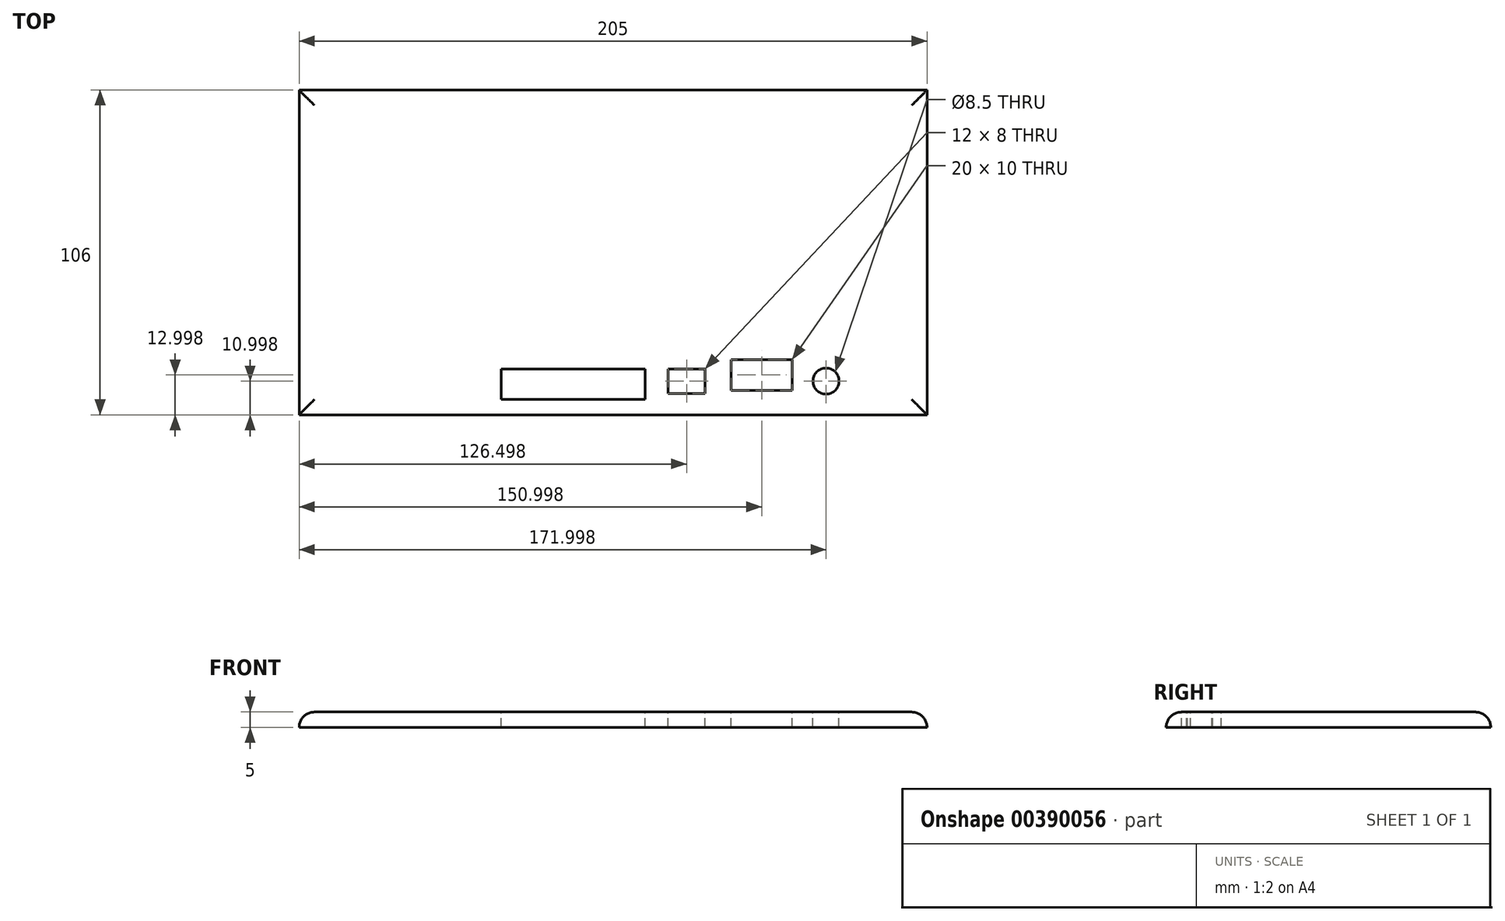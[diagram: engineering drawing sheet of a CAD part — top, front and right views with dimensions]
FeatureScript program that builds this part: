
annotation { "Feature Type Name" : "Feature", "Feature Type Description" : "" }
export const myFeature = defineFeature(function(context is Context, id is Id, definition is map)
    precondition{}
    {
        {
            var Q0;
            Q0=qCreatedBy(makeId("Top.planeOp"),FACE);
            var sketch = newSketch(context, id + "F0", { "sketchPlane" : qUnion([Q0])});
            skLineSegment(sketch, "E0.bottom", {"start": v(-821.61, -528.85) * mm, "end": v(-616.61, -528.85) * mm});
            skLineSegment(sketch, "E0.top", {"start": v(-821.61, -422.85) * mm, "end": v(-616.61, -422.85) * mm});
            skLineSegment(sketch, "E0.left", {"start": v(-821.61, -528.85) * mm, "end": v(-821.61, -422.85) * mm});
            skLineSegment(sketch, "E0.right", {"start": v(-616.61, -528.85) * mm, "end": v(-616.61, -422.85) * mm});
            skSolve(sketch);
        }
        {
            var Q0;
            Q0=makeQuery(id+"F0.imprint","IMPRINT",FACE,{"disambiguationData":[TD([[makeQuery(id+"F0.imprint","IMPRINT",EDGE,{"derivedFrom":sQuery(id+"F0.wireOp",EDGE,"E0.bottom")}),1.0]])]});
            extrude(context, id + "F1", {"entities" : qUnion([Q0]), "depth" : 5 * mm});
        }
        {
            var Q0;
            Q0=makeQuery(id+"F1.opExtrude","CAP_FACE",FACE,{"disambiguationData":[OSD([sQuery(id+"F0.wireOp",EDGE,"E0.bottom"),sQuery(id+"F0.wireOp",EDGE,"E0.top"),sQuery(id+"F0.wireOp",EDGE,"E0.left"),sQuery(id+"F0.wireOp",EDGE,"E0.right")])],"isStart":false});
            var sketch = newSketch(context, id + "F2", { "sketchPlane" : qUnion([Q0])});
            skCircle(sketch, "E1", {"center": v(-649.61, -517.85) * mm, "radius": 4.25 * mm});
            skSolve(sketch);
        }
        {
            var Q0;
            Q0=makeQuery(id+"F2.imprint","IMPRINT",FACE,{"disambiguationData":[TD([[makeQuery(id+"F2.imprint","IMPRINT",EDGE,{"derivedFrom":sQuery(id+"F2.wireOp",EDGE,"E1")}),1.0]])]});
            extrude(context, id + "F3", {"entities" : qUnion([Q0]), "operationType" : NewBodyOperationType.REMOVE, "oppositeDirection" : true, "depth" : 500 * mm});
        }
        {
            var Q0;
            Q0=makeQuery(id+"F1.opExtrude","CAP_FACE",FACE,{"disambiguationData":[OSD([sQuery(id+"F0.wireOp",EDGE,"E0.bottom"),sQuery(id+"F0.wireOp",EDGE,"E0.top"),sQuery(id+"F0.wireOp",EDGE,"E0.left"),sQuery(id+"F0.wireOp",EDGE,"E0.right")])],"isStart":false});
            var sketch = newSketch(context, id + "F4", { "sketchPlane" : qUnion([Q0])});
            skLineSegment(sketch, "E2.bottom", {"start": v(-680.61, -510.85) * mm, "end": v(-660.61, -510.85) * mm});
            skLineSegment(sketch, "E2.top", {"start": v(-680.61, -520.85) * mm, "end": v(-660.61, -520.85) * mm});
            skLineSegment(sketch, "E2.left", {"start": v(-680.61, -510.85) * mm, "end": v(-680.61, -520.85) * mm});
            skLineSegment(sketch, "E2.right", {"start": v(-660.61, -510.85) * mm, "end": v(-660.61, -520.85) * mm});
            skSolve(sketch);
        }
        {
            var Q0;
            Q0=makeQuery(id+"F4.imprint","IMPRINT",FACE,{"disambiguationData":[TD([[makeQuery(id+"F4.imprint","IMPRINT",EDGE,{"derivedFrom":sQuery(id+"F4.wireOp",EDGE,"E2.bottom")}),-1.0]])]});
            extrude(context, id + "F5", {"entities" : qUnion([Q0]), "operationType" : NewBodyOperationType.REMOVE, "oppositeDirection" : true, "depth" : 500 * mm});
        }
        {
            var Q0;
            Q0=makeQuery(id+"F1.opExtrude","CAP_FACE",FACE,{"disambiguationData":[OSD([sQuery(id+"F0.wireOp",EDGE,"E0.bottom"),sQuery(id+"F0.wireOp",EDGE,"E0.top"),sQuery(id+"F0.wireOp",EDGE,"E0.left"),sQuery(id+"F0.wireOp",EDGE,"E0.right")])],"isStart":false});
            var sketch = newSketch(context, id + "F6", { "sketchPlane" : qUnion([Q0])});
            skLineSegment(sketch, "E3.bottom", {"start": v(-701.11, -521.85) * mm, "end": v(-689.11, -521.85) * mm});
            skLineSegment(sketch, "E3.top", {"start": v(-701.11, -513.85) * mm, "end": v(-689.11, -513.85) * mm});
            skLineSegment(sketch, "E3.left", {"start": v(-701.11, -521.85) * mm, "end": v(-701.11, -513.85) * mm});
            skLineSegment(sketch, "E3.right", {"start": v(-689.11, -521.85) * mm, "end": v(-689.11, -513.85) * mm});
            skSolve(sketch);
        }
        {
            var Q0;
            Q0=makeQuery(id+"F6.imprint","IMPRINT",FACE,{"disambiguationData":[TD([[makeQuery(id+"F6.imprint","IMPRINT",EDGE,{"derivedFrom":sQuery(id+"F6.wireOp",EDGE,"E3.bottom")}),1.0]])]});
            extrude(context, id + "F7", {"entities" : qUnion([Q0]), "operationType" : NewBodyOperationType.REMOVE, "oppositeDirection" : true, "depth" : 500 * mm});
        }
        {
            var Q0;
            Q0=makeQuery(id+"F1.opExtrude","CAP_EDGE",EDGE,{"disambiguationData":[OSD([sQuery(id+"F0.wireOp",EDGE,"E0.left")])],"isStart":false});
            var Q1;
            Q1=makeQuery(id+"F1.opExtrude","CAP_EDGE",EDGE,{"disambiguationData":[OSD([sQuery(id+"F0.wireOp",EDGE,"E0.bottom")])],"isStart":false});
            var Q2;
            Q2=makeQuery(id+"F1.opExtrude","CAP_EDGE",EDGE,{"disambiguationData":[OSD([sQuery(id+"F0.wireOp",EDGE,"E0.right")])],"isStart":false});
            var Q3;
            Q3=makeQuery(id+"F1.opExtrude","CAP_EDGE",EDGE,{"disambiguationData":[OSD([sQuery(id+"F0.wireOp",EDGE,"E0.top")])],"isStart":false});
            fillet(context, id + "F8", {"entities" : qUnion([Q0, Q1, Q2, Q3]), "radius" : 5 * mm, "tangentPropagation" : true, "allowEdgeOverflow" : false});
        }
        {
            var Q0;
            Q0=makeQuery(id+"F1.opExtrude","CAP_FACE",FACE,{"disambiguationData":[OSD([sQuery(id+"F0.wireOp",EDGE,"E0.bottom"),sQuery(id+"F0.wireOp",EDGE,"E0.top"),sQuery(id+"F0.wireOp",EDGE,"E0.left"),sQuery(id+"F0.wireOp",EDGE,"E0.right")])],"isStart":false});
            var sketch = newSketch(context, id + "F9", { "sketchPlane" : qUnion([Q0])});
            skLineSegment(sketch, "E4.bottom", {"start": v(-755.61, -513.85) * mm, "end": v(-708.61, -513.85) * mm});
            skLineSegment(sketch, "E4.top", {"start": v(-755.61, -523.85) * mm, "end": v(-708.61, -523.85) * mm});
            skLineSegment(sketch, "E4.left", {"start": v(-755.61, -513.85) * mm, "end": v(-755.61, -523.85) * mm});
            skLineSegment(sketch, "E4.right", {"start": v(-708.61, -513.85) * mm, "end": v(-708.61, -523.85) * mm});
            skSolve(sketch);
        }
        {
            var Q0;
            Q0=makeQuery(id+"F9.imprint","IMPRINT",FACE,{"disambiguationData":[TD([[makeQuery(id+"F9.imprint","IMPRINT",EDGE,{"derivedFrom":sQuery(id+"F9.wireOp",EDGE,"E4.bottom")}),-1.0]])]});
            extrude(context, id + "F10", {"entities" : qUnion([Q0]), "operationType" : NewBodyOperationType.REMOVE, "oppositeDirection" : true, "depth" : 500 * mm});
        }
    });
